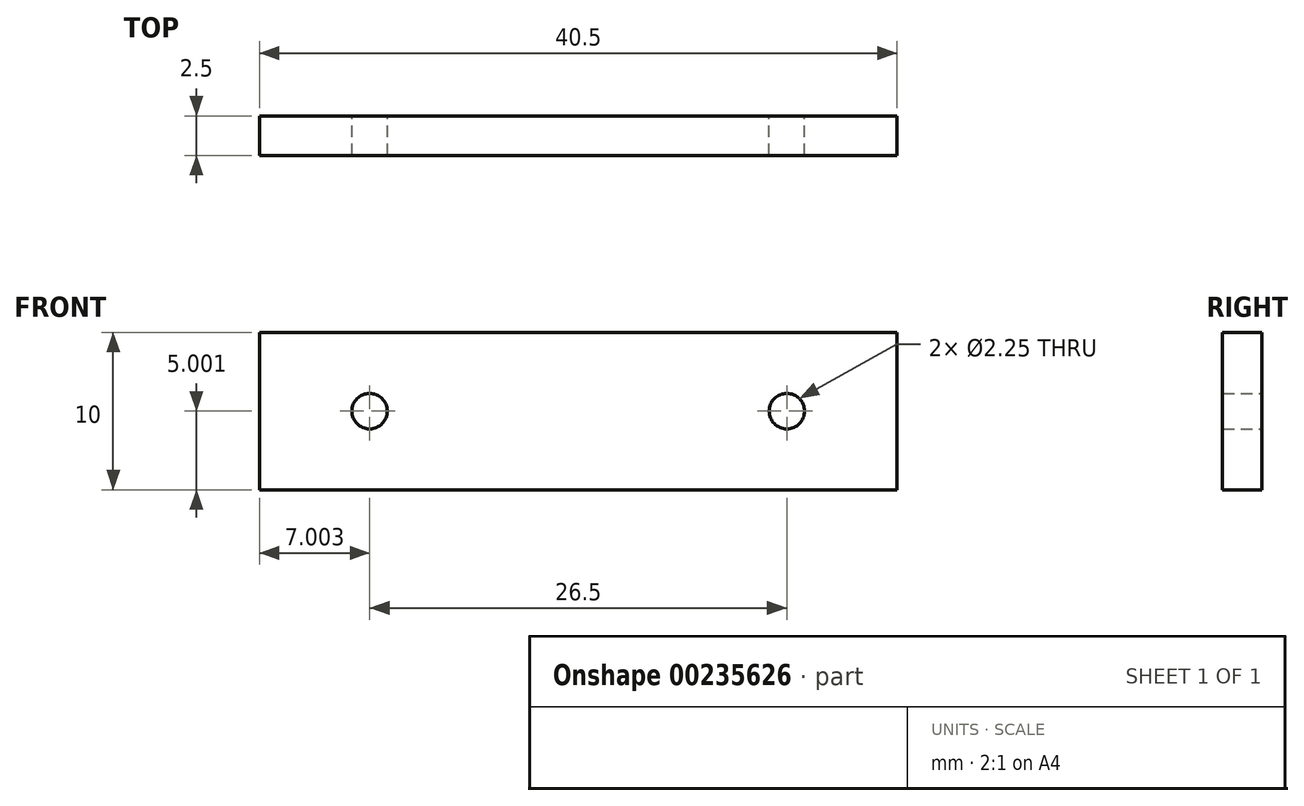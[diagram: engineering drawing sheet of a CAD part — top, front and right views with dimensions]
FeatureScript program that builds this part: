
annotation { "Feature Type Name" : "Feature", "Feature Type Description" : "" }
export const myFeature = defineFeature(function(context is Context, id is Id, definition is map)
    precondition{}
    {
        {
            var Q0;
            Q0=qCreatedBy(makeId("Front.planeOp"),FACE);
            var sketch = newSketch(context, id + "F0", { "sketchPlane" : qUnion([Q0])});
            skLineSegment(sketch, "E0.bottom", {"start": v(-19.93, -14.73) * mm, "end": v(20.57, -14.73) * mm});
            skLineSegment(sketch, "E0.top", {"start": v(-19.93, -24.73) * mm, "end": v(20.57, -24.73) * mm});
            skLineSegment(sketch, "E0.left", {"start": v(-19.93, -14.73) * mm, "end": v(-19.93, -24.73) * mm});
            skLineSegment(sketch, "E0.right", {"start": v(20.57, -14.73) * mm, "end": v(20.57, -24.73) * mm});
            skLineSegment(sketch, "E1", {"start": v(-19.93, -19.73) * mm, "end": v(-12.93, -19.73) * mm, "construction": true});
            skLineSegment(sketch, "E2", {"start": v(20.57, -19.73) * mm, "end": v(13.57, -19.73) * mm, "construction": true});
            skCircle(sketch, "E3", {"center": v(-12.93, -19.73) * mm, "radius": 1.13 * mm});
            skCircle(sketch, "E4", {"center": v(13.57, -19.73) * mm, "radius": 1.13 * mm});
            skSolve(sketch);
        }
        {
            var Q0;
            Q0=makeQuery(id+"F0.imprint","IMPRINT",FACE,{"disambiguationData":[TD([[makeQuery(id+"F0.imprint","IMPRINT",EDGE,{"derivedFrom":sQuery(id+"F0.wireOp",EDGE,"E0.bottom")}),-1.0]])]});
            extrude(context, id + "F1", {"entities" : qUnion([Q0]), "depth" : 2.5 * mm});
        }
    });
